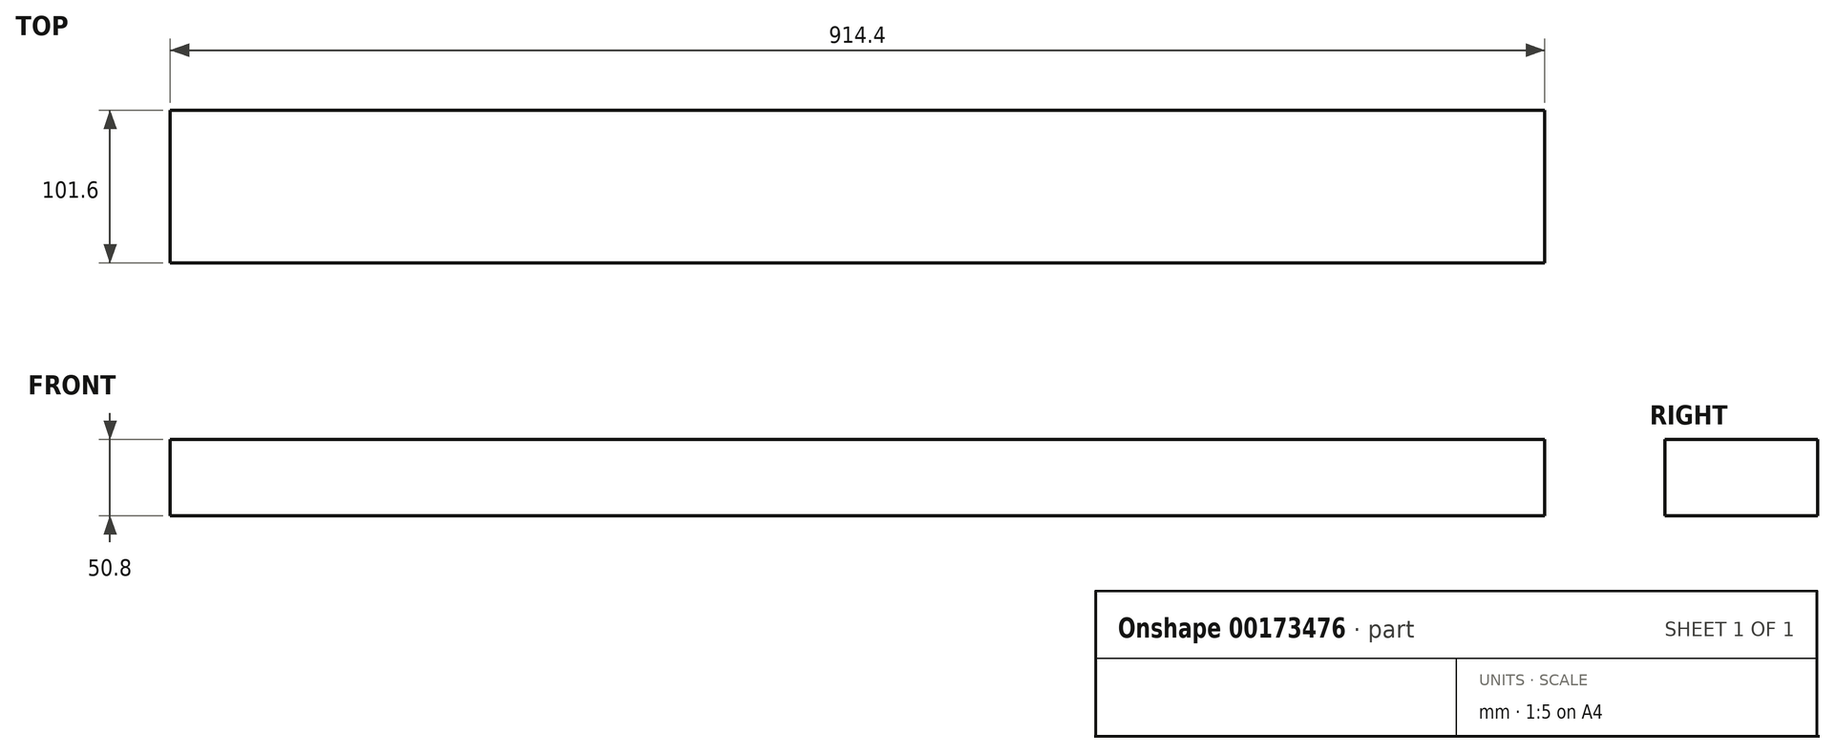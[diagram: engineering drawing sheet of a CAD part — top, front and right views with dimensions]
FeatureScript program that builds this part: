
annotation { "Feature Type Name" : "Feature", "Feature Type Description" : "" }
export const myFeature = defineFeature(function(context is Context, id is Id, definition is map)
    precondition{}
    {
        {
            var Q0;
            Q0=qCreatedBy(makeId("Right.planeOp"),FACE);
            var sketch = newSketch(context, id + "F0", { "sketchPlane" : qUnion([Q0])});
            skLineSegment(sketch, "E0.bottom", {"start": v(50.8, 25.4) * mm, "end": v(-50.8, 25.4) * mm});
            skLineSegment(sketch, "E0.top", {"start": v(50.8, -25.4) * mm, "end": v(-50.8, -25.4) * mm});
            skLineSegment(sketch, "E0.left", {"start": v(50.8, 25.4) * mm, "end": v(50.8, -25.4) * mm});
            skLineSegment(sketch, "E0.right", {"start": v(-50.8, 25.4) * mm, "end": v(-50.8, -25.4) * mm});
            skPoint(sketch, "E0.middle", {"position": v(0, 0) * mm});
            skSolve(sketch);
        }
        {
            var Q0;
            Q0=makeQuery(id+"F0.imprint","IMPRINT",FACE,{"disambiguationData":[TD([[makeQuery(id+"F0.imprint","IMPRINT",EDGE,{"derivedFrom":sQuery(id+"F0.wireOp",EDGE,"E0.bottom")}),1.0]])]});
            extrude(context, id + "F1", {"entities" : qUnion([Q0]), "depth" : 914.4 * mm});
        }
    });
